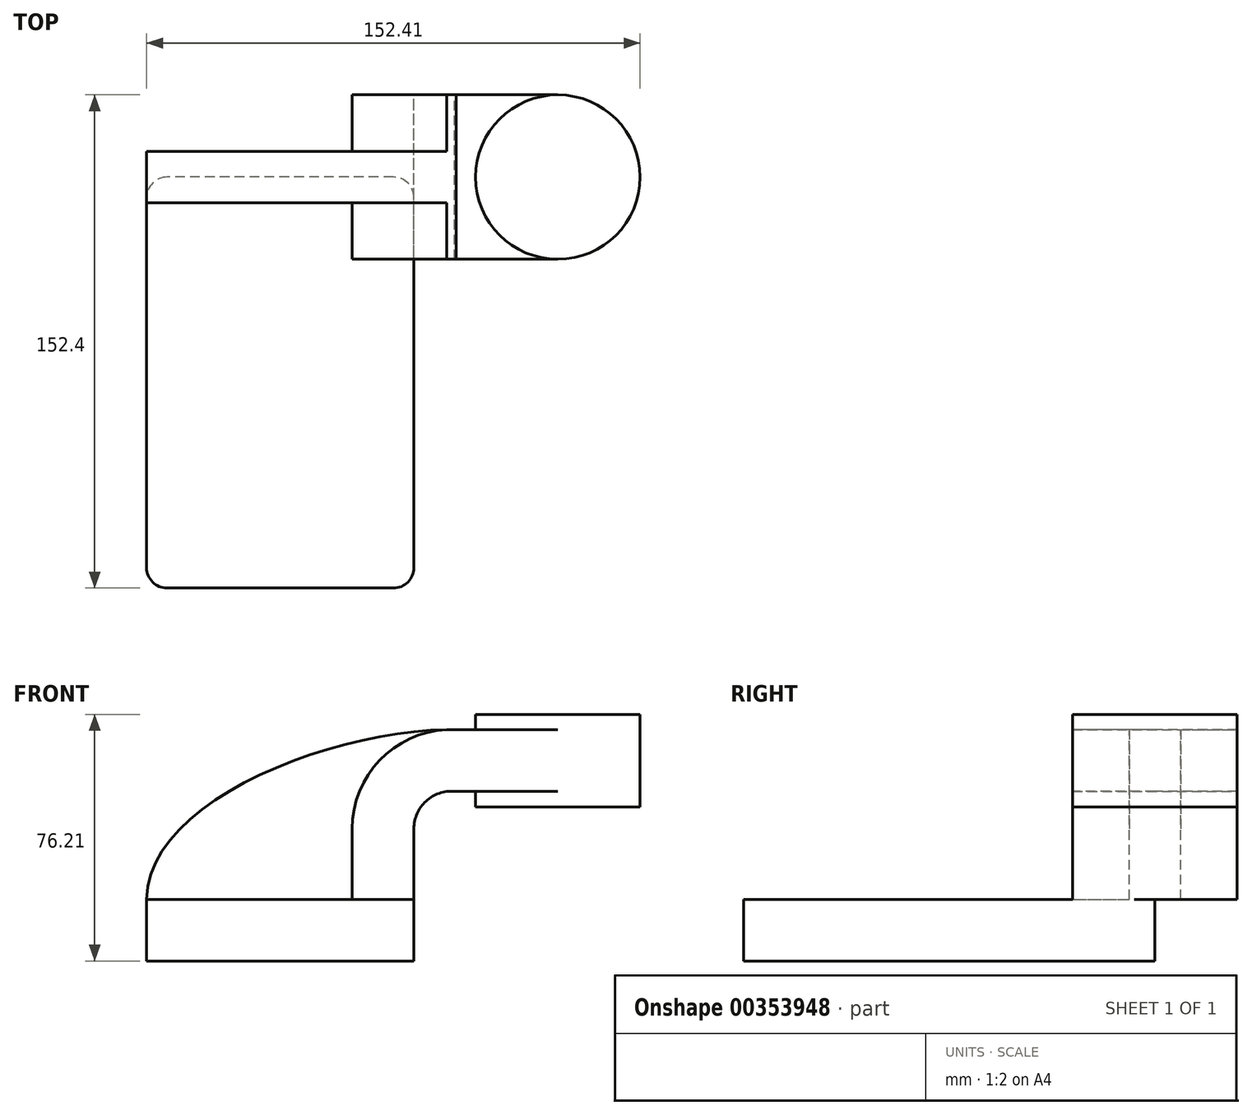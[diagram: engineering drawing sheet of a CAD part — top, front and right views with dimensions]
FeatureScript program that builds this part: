
annotation { "Feature Type Name" : "Feature", "Feature Type Description" : "" }
export const myFeature = defineFeature(function(context is Context, id is Id, definition is map)
    precondition{}
    {
        {
            var Q0;
            Q0=qCreatedBy(makeId("Front.planeOp"),FACE);
            var sketch = newSketch(context, id + "F0", { "sketchPlane" : qUnion([Q0])});
            skLineSegment(sketch, "E0.bottom", {"start": v(41.27, 9.53) * mm, "end": v(-41.28, 9.53) * mm});
            skLineSegment(sketch, "E0.top", {"start": v(41.28, -9.52) * mm, "end": v(-41.27, -9.52) * mm});
            skLineSegment(sketch, "E0.left", {"start": v(41.28, 9.53) * mm, "end": v(41.28, -9.52) * mm});
            skLineSegment(sketch, "E0.right", {"start": v(-41.28, 9.53) * mm, "end": v(-41.28, -9.52) * mm});
            skPoint(sketch, "E0.middle", {"position": v(0, 0) * mm});
            skLineSegment(sketch, "E1.bottom", {"start": v(111.12, 66.68) * mm, "end": v(60.32, 66.68) * mm});
            skLineSegment(sketch, "E1.top", {"start": v(111.12, 38.1) * mm, "end": v(60.32, 38.1) * mm});
            skLineSegment(sketch, "E1.left", {"start": v(111.12, 66.67) * mm, "end": v(111.12, 38.1) * mm});
            skLineSegment(sketch, "E1.right", {"start": v(60.32, 66.67) * mm, "end": v(60.32, 38.1) * mm});
            skPoint(sketch, "E1.middle", {"position": v(85.72, 52.39) * mm});
            skLineSegment(sketch, "E2", {"start": v(41.27, 9.53) * mm, "end": v(41.27, 31.34) * mm});
            skArc(sketch, "E3", {"start": v(41.28, 31.34) * mm, "mid": v(45, 39.85) * mm, "end": v(53.79, 42.88) * mm});
            skLineSegment(sketch, "E4", {"start": v(53.79, 42.88) * mm, "end": v(110.54, 42.88) * mm});
            skLineSegment(sketch, "E5.0", {"start": v(54.38, 61.93) * mm, "end": v(110.54, 61.93) * mm});
            skArc(sketch, "E5.1", {"start": v(22.23, 31.34) * mm, "mid": v(31.74, 53.53) * mm, "end": v(54.38, 61.93) * mm});
            skLineSegment(sketch, "E5.2", {"start": v(22.22, 9.53) * mm, "end": v(22.22, 31.34) * mm});
            skLineSegment(sketch, "E6", {"start": v(85.72, 38.1) * mm, "end": v(85.72, 66.68) * mm});
            skFitSpline(sketch, "E7", {"points": [v(-41.28, 9.52) * mm, v(54.38, 61.93) * mm], "startDerivative": vector(0.18, 92.04) * mm, "endDerivative": vector(110.42, -1.92) * mm});
            skSolve(sketch);
        }
        {
            var Q0;
            Q0=makeQuery(id+"F0.imprint","IMPRINT",FACE,{"disambiguationData":[TD([[makeQuery(id+"F0.imprint","IMPRINT",EDGE,{"derivedFrom":sQuery(id+"F0.wireOp",EDGE,"E0.top")}),-1.0]])]});
            extrude(context, id + "F1", {"entities" : qUnion([Q0]), "depth" : 127 * mm});
        }
        {
            var Q0;
            {var subQ1=sQuery(id+"F0.wireOp",EDGE,"E2");Q0=makeQuery(id+"F0.imprint","IMPRINT",FACE,{"disambiguationData":[TD([[makeQuery(id+"F0.imprint","IMPRINT",EDGE,{"derivedFrom":subQ1}),1.0]])]});}
            var Q1;
            {var subQ0=sQuery(id+"F0.wireOp",EDGE,"E5.0");var subQ1=sQuery(id+"F0.wireOp",EDGE,"E1.right");var subQ2=makeQuery(id+"F0.imprint","INTERSECT",VERTEX,{"derivedFrom":[subQ1,subQ0]});Q1=makeQuery(id+"F0.imprint","IMPRINT",FACE,{"disambiguationData":[TD([[makeQuery(id+"F0.imprint","IMPRINT",EDGE,{"disambiguationData":[TD([[subQ2,-1.0]])],"derivedFrom":subQ1}),1.0]])]});}
            extrude(context, id + "F2", {"entities" : qUnion([Q0, Q1]), "operationType" : NewBodyOperationType.ADD, "endBound" : BoundingType.SYMMETRIC, "depth" : 50.8 * mm});
        }
        {
            var Q0;
            {var subQ3=sQuery(id+"F0.wireOp",EDGE,"E5.2");Q0=makeQuery(id+"F0.imprint","IMPRINT",FACE,{"disambiguationData":[TD([[makeQuery(id+"F0.imprint","IMPRINT",EDGE,{"derivedFrom":subQ3}),1.0]])]});}
            extrude(context, id + "F3", {"entities" : qUnion([Q0]), "operationType" : NewBodyOperationType.ADD, "endBound" : BoundingType.SYMMETRIC, "depth" : 15.88 * mm});
        }
        {
            var Q0;
            {var subQ0=sQuery(id+"F0.wireOp",EDGE,"E1.left");Q0=makeQuery(id+"F0.imprint","IMPRINT",FACE,{"disambiguationData":[TD([[makeQuery(id+"F0.imprint","IMPRINT",EDGE,{"derivedFrom":subQ0}),-1.0]])]});}
            var Q1;
            Q1=sQuery(id+"F0.wireOp",EDGE,"E6");
            revolve(context, id + "F4", {"operationType" : NewBodyOperationType.ADD, "entities" : qUnion([Q0]), "axis" : qUnion([Q1]), "revolveType" : RevolveType.FULL});
        }
        {
            var Q0;
            Q0=makeQuery(id+"F1.opExtrude","CAP_EDGE",EDGE,{"disambiguationData":[OSD([sQuery(id+"F0.wireOp",EDGE,"E0.left")])],"isStart":false});
            var Q1;
            Q1=makeQuery(id+"F1.opExtrude","CAP_EDGE",EDGE,{"disambiguationData":[OSD([sQuery(id+"F0.wireOp",EDGE,"E0.right")])],"isStart":false});
            var Q2;
            Q2=makeQuery(id+"F1.opExtrude","CAP_EDGE",EDGE,{"disambiguationData":[OSD([sQuery(id+"F0.wireOp",EDGE,"E0.left")])],"isStart":true});
            var Q3;
            Q3=makeQuery(id+"F1.opExtrude","CAP_EDGE",EDGE,{"disambiguationData":[OSD([sQuery(id+"F0.wireOp",EDGE,"E0.right")])],"isStart":true});
            fillet(context, id + "F5", {"entities" : qUnion([Q0, Q1, Q2, Q3]), "radius" : 6.35 * mm, "tangentPropagation" : true, "allowEdgeOverflow" : false});
        }
    });
